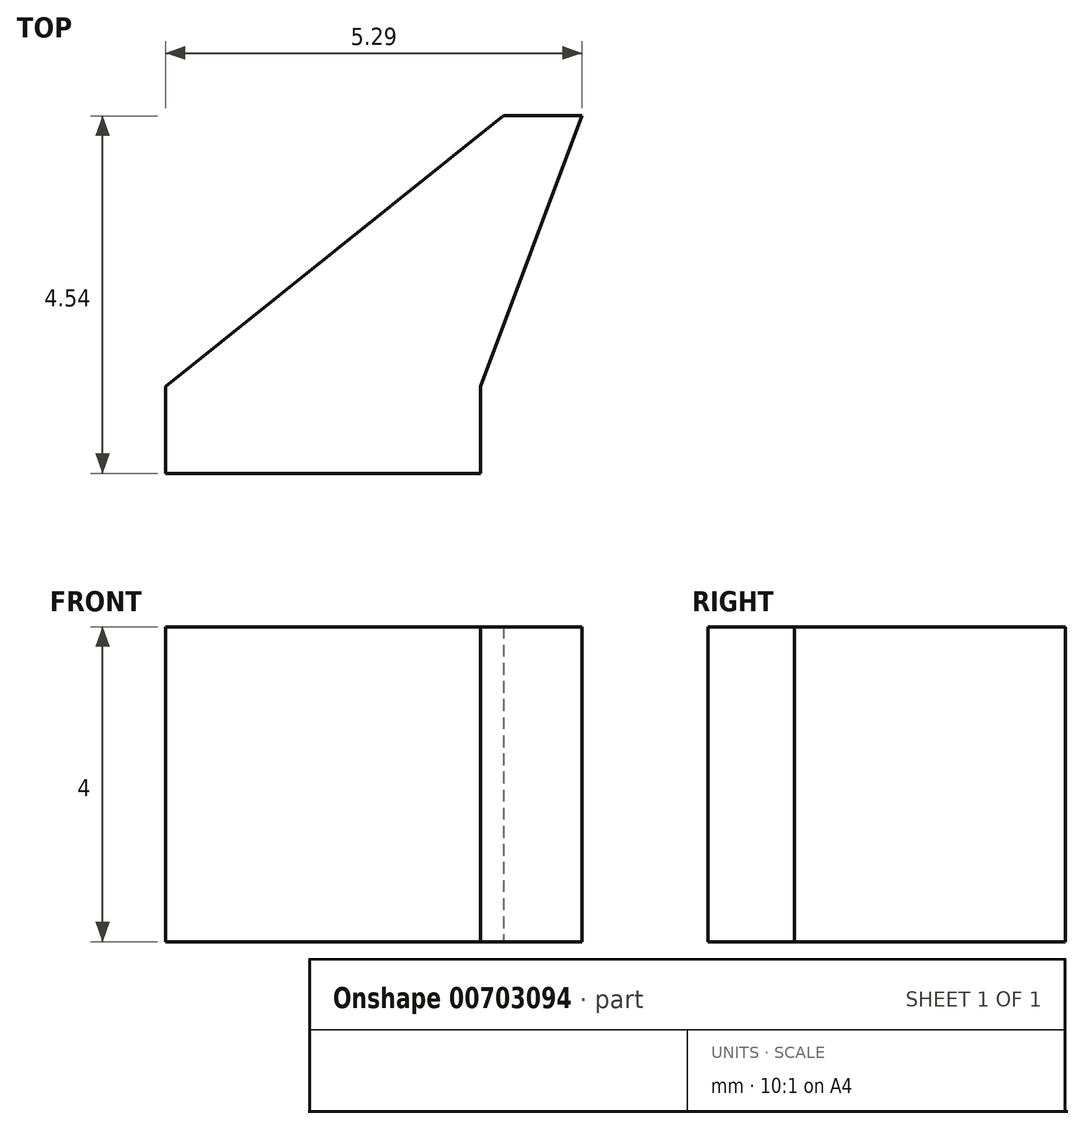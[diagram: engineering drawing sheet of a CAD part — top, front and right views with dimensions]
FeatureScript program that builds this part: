
annotation { "Feature Type Name" : "Feature", "Feature Type Description" : "" }
export const myFeature = defineFeature(function(context is Context, id is Id, definition is map)
    precondition{}
    {
        {
            var Q0;
            Q0=qCreatedBy(makeId("Top.planeOp"),FACE);
            var sketch = newSketch(context, id + "F0", { "sketchPlane" : qUnion([Q0])});
            skLineSegment(sketch, "E0", {"start": v(0, 0) * mm, "end": v(4, 0) * mm});
            skLineSegment(sketch, "E1", {"start": v(0, 0) * mm, "end": v(4.3, 3.44) * mm});
            skLineSegment(sketch, "E2", {"start": v(4.3, 3.44) * mm, "end": v(5.3, 3.44) * mm});
            skLineSegment(sketch, "E3", {"start": v(5.3, 3.44) * mm, "end": v(4, 0) * mm});
            skSolve(sketch);
        }
        {
            var Q0;
            Q0=makeQuery(id+"F0.imprint","IMPRINT",FACE,{"disambiguationData":[TD([[makeQuery(id+"F0.imprint","IMPRINT",EDGE,{"derivedFrom":sQuery(id+"F0.wireOp",EDGE,"E0")}),1.0]])]});
            extrude(context, id + "F1", {"entities" : qUnion([Q0]), "depth" : 4 * mm, "offsetDistance" : 25 * mm});
        }
        {
            var Q0;
            Q0=makeQuery(id+"F1.opExtrude","SWEPT_FACE",FACE,{"disambiguationData":[OSD([sQuery(id+"F0.wireOp",EDGE,"E0")])]});
            extrude(context, id + "F2", {"entities" : qUnion([Q0]), "operationType" : NewBodyOperationType.ADD, "depth" : 1.1 * mm, "offsetDistance" : 25 * mm});
        }
    });
